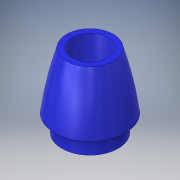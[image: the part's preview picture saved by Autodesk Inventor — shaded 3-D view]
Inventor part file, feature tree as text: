
AUTODESK INVENTOR PART (.ipt)
format: ipt  version: 2018 (Build 220112000, 112)  size: 152,064 bytes
history: native  units: in
note: dims shown in document units (in); Inventor stores cm internally (conversion verified against a paired STEP export)
features: sketch x2, revolve x1, extrude x1
ambient origin geometry x8: Origin, YZ Plane, XZ Plane, XY Plane, X Axis, Y Axis, Z Axis, Center Point
bodies: Solid1 (feature_tree)
feature tree (4):
  revolve  "Revolution1"  [1 undecoded]
  extrude  "Extrusion1"  TaperAngle=90.0deg  [1 undecoded]
  sketch  "Sketch1"  dims[d0=1.5625in d1=5.0in]
  sketch  "Sketch2"  dims[d3=14.0in d4=90.0deg d5=1.5in d6=1.5in d7=2.5in d9=0.75in d10=0.25in d11=0.75in d12=0.25in d13=0.25in d14=0.75in d15=0.0in]
note: 2 required parameter values undecoded (feature->parameter linkage not recoverable at this tier; creation-order binding heuristic only, values carry confidence <= 0.55)